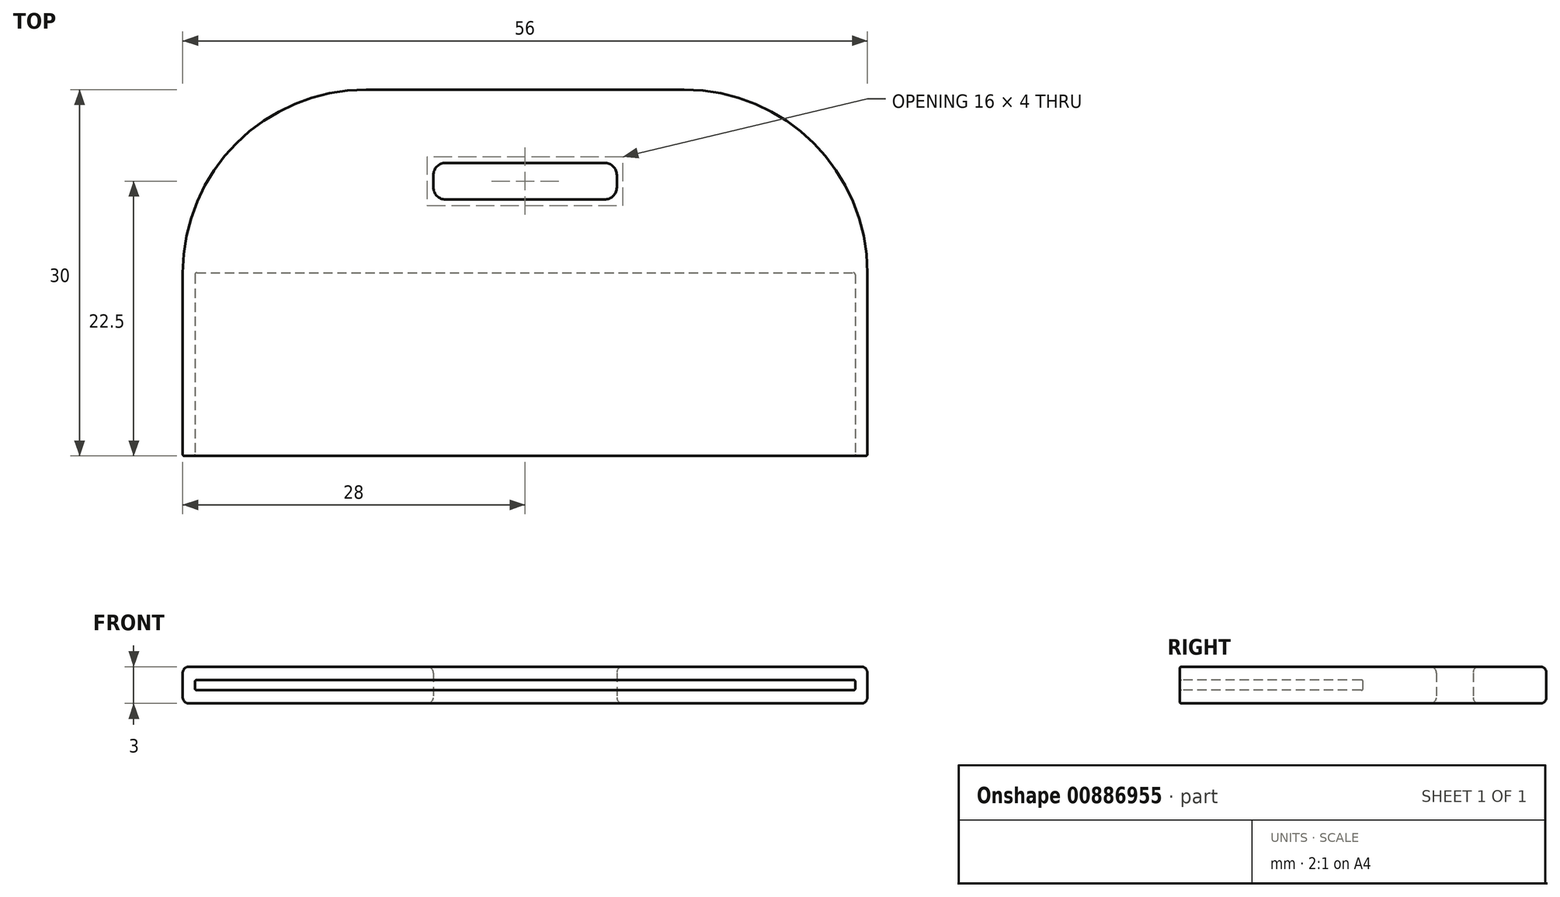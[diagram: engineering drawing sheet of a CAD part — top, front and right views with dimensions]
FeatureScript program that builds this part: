
annotation { "Feature Type Name" : "Feature", "Feature Type Description" : "" }
export const myFeature = defineFeature(function(context is Context, id is Id, definition is map)
    precondition{}
    {
        {
            var Q0;
            Q0=qCreatedBy(makeId("Top.planeOp"),FACE);
            var sketch = newSketch(context, id + "F0", { "sketchPlane" : qUnion([Q0])});
            skLineSegment(sketch, "E0.bottom", {"start": v(-28, 30) * mm, "end": v(28, 30) * mm});
            skLineSegment(sketch, "E0.top", {"start": v(-28, 0) * mm, "end": v(28, 0) * mm});
            skLineSegment(sketch, "E0.left", {"start": v(-28, 30) * mm, "end": v(-28, 0) * mm});
            skLineSegment(sketch, "E0.right", {"start": v(28, 30) * mm, "end": v(28, 0) * mm});
            skLineSegment(sketch, "E1.bottom", {"start": v(-7.5, 24) * mm, "end": v(7.5, 24) * mm});
            skLineSegment(sketch, "E1.top", {"start": v(-7.5, 21) * mm, "end": v(7.5, 21) * mm});
            skLineSegment(sketch, "E1.left", {"start": v(-7.5, 24) * mm, "end": v(-7.5, 21) * mm});
            skLineSegment(sketch, "E1.right", {"start": v(7.5, 24) * mm, "end": v(7.5, 21) * mm});
            skLineSegment(sketch, "E2", {"start": v(-7.5, 22.5) * mm, "end": v(7.5, 22.5) * mm, "construction": true});
            skLineSegment(sketch, "E3", {"start": v(0, 22.5) * mm, "end": v(0, 0) * mm, "construction": true});
            skSolve(sketch);
        }
        {
            var Q0;
            Q0 = qSketchRegion(id + "F0", true);
            extrude(context, id + "F1", {"entities" : qUnion([Q0]), "depth" : 3 * mm, "offsetDistance" : 25 * mm});
        }
        {
            var Q0;
            Q0=makeQuery(id+"F1.opExtrude","SWEPT_EDGE",EDGE,{"disambiguationData":[OSD([sQuery(id+"F0.wireOp",EDGE,"E0.bottom"),sQuery(id+"F0.wireOp",EDGE,"E0.right")])]});
            var Q1;
            Q1=makeQuery(id+"F1.opExtrude","SWEPT_EDGE",EDGE,{"disambiguationData":[OSD([sQuery(id+"F0.wireOp",EDGE,"E0.bottom"),sQuery(id+"F0.wireOp",EDGE,"E0.left")])]});
            fillet(context, id + "F2", {"entities" : qUnion([Q0, Q1]), "radius" : 15 * mm, "tangentPropagation" : true, "allowEdgeOverflow" : false});
        }
        {
            var Q0;
            Q0=makeQuery(id+"F1.opExtrude","SWEPT_EDGE",EDGE,{"disambiguationData":[OSD([sQuery(id+"F0.wireOp",EDGE,"E1.bottom"),sQuery(id+"F0.wireOp",EDGE,"E1.left")])]});
            var Q1;
            Q1=makeQuery(id+"F1.opExtrude","SWEPT_EDGE",EDGE,{"disambiguationData":[OSD([sQuery(id+"F0.wireOp",EDGE,"E1.top"),sQuery(id+"F0.wireOp",EDGE,"E1.right")])]});
            var Q2;
            Q2=makeQuery(id+"F1.opExtrude","SWEPT_EDGE",EDGE,{"disambiguationData":[OSD([sQuery(id+"F0.wireOp",EDGE,"E1.bottom"),sQuery(id+"F0.wireOp",EDGE,"E1.right")])]});
            var Q3;
            Q3=makeQuery(id+"F1.opExtrude","SWEPT_EDGE",EDGE,{"disambiguationData":[OSD([sQuery(id+"F0.wireOp",EDGE,"E1.top"),sQuery(id+"F0.wireOp",EDGE,"E1.left")])]});
            fillet(context, id + "F3", {"entities" : qUnion([Q0, Q1, Q2, Q3]), "radius" : 1 * mm, "tangentPropagation" : true, "allowEdgeOverflow" : false});
        }
        {
            var Q0;
            Q0=makeQuery(id+"F1.opExtrude","CAP_EDGE",EDGE,{"disambiguationData":[OSD([sQuery(id+"F0.wireOp",EDGE,"E0.bottom")])],"isStart":false});
            var Q1;
            Q1=makeQuery(id+"F1.opExtrude","CAP_EDGE",EDGE,{"disambiguationData":[OSD([sQuery(id+"F0.wireOp",EDGE,"E0.bottom")])],"isStart":true});
            var Q2;
            Q2=makeQuery(id+"F1.opExtrude","CAP_EDGE",EDGE,{"disambiguationData":[OSD([sQuery(id+"F0.wireOp",EDGE,"E1.bottom")])],"isStart":false});
            var Q3;
            Q3=makeQuery(id+"F1.opExtrude","CAP_EDGE",EDGE,{"disambiguationData":[OSD([sQuery(id+"F0.wireOp",EDGE,"E1.bottom")])],"isStart":true});
            fillet(context, id + "F4", {"entities" : qUnion([Q0, Q1, Q2, Q3]), "radius" : .5 * mm, "tangentPropagation" : true, "allowEdgeOverflow" : false});
        }
        {
            var Q0;
            Q0=makeQuery(id+"F1.opExtrude","SWEPT_FACE",FACE,{"disambiguationData":[OSD([sQuery(id+"F0.wireOp",EDGE,"E0.top")])]});
            var sketch = newSketch(context, id + "F5", { "sketchPlane" : qUnion([Q0])});
            skLineSegment(sketch, "E4.bottom", {"start": v(-27, 1.07) * mm, "end": v(27, 1.07) * mm});
            skLineSegment(sketch, "E4.top", {"start": v(-27, 1.93) * mm, "end": v(27, 1.93) * mm});
            skLineSegment(sketch, "E4.left", {"start": v(-27, 1.07) * mm, "end": v(-27, 1.93) * mm});
            skLineSegment(sketch, "E4.right", {"start": v(27, 1.07) * mm, "end": v(27, 1.93) * mm});
            skLineSegment(sketch, "E5", {"start": v(0, 0) * mm, "end": v(0, 1.07) * mm, "construction": true});
            skLineSegment(sketch, "E6", {"start": v(-28, 1.5) * mm, "end": v(-27, 1.5) * mm, "construction": true});
            skSolve(sketch);
        }
        {
            var Q0;
            Q0=makeQuery(id+"F5.imprint","IMPRINT",FACE,{"disambiguationData":[TD([[makeQuery(id+"F5.imprint","IMPRINT",EDGE,{"derivedFrom":sQuery(id+"F5.wireOp",EDGE,"E4.bottom")}),1.0]])]});
            extrude(context, id + "F6", {"entities" : qUnion([Q0]), "operationType" : NewBodyOperationType.REMOVE, "oppositeDirection" : true, "depth" : 15 * mm, "offsetDistance" : 25 * mm});
        }
        {
            var Q0;
            Q0=makeQuery(id+"F6.boolean.opBoolean","COPY",EDGE,{"derivedFrom":makeQuery(id+"F6.opExtrude","SWEPT_EDGE",EDGE,{"disambiguationData":[OSD([sQuery(id+"F5.wireOp",EDGE,"E4.bottom"),sQuery(id+"F5.wireOp",EDGE,"E4.left")])]})});
            var Q1;
            Q1=makeQuery(id+"F6.boolean.opBoolean","COPY",EDGE,{"derivedFrom":makeQuery(id+"F6.opExtrude","CAP_EDGE",EDGE,{"disambiguationData":[OSD([sQuery(id+"F5.wireOp",EDGE,"E4.bottom")])],"isStart":false})});
            var Q2;
            Q2=makeQuery(id+"F6.boolean.opBoolean","COPY",EDGE,{"derivedFrom":makeQuery(id+"F6.opExtrude","CAP_EDGE",EDGE,{"disambiguationData":[OSD([sQuery(id+"F5.wireOp",EDGE,"E4.left")])],"isStart":false})});
            var Q3;
            Q3=makeQuery(id+"F6.boolean.opBoolean","COPY",EDGE,{"derivedFrom":makeQuery(id+"F6.opExtrude","SWEPT_EDGE",EDGE,{"disambiguationData":[OSD([sQuery(id+"F5.wireOp",EDGE,"E4.top"),sQuery(id+"F5.wireOp",EDGE,"E4.left")])]})});
            var Q4;
            Q4=makeQuery(id+"F6.boolean.opBoolean","COPY",EDGE,{"derivedFrom":makeQuery(id+"F6.opExtrude","CAP_EDGE",EDGE,{"disambiguationData":[OSD([sQuery(id+"F5.wireOp",EDGE,"E4.top")])],"isStart":false})});
            var Q5;
            Q5=makeQuery(id+"F6.boolean.opBoolean","COPY",EDGE,{"derivedFrom":makeQuery(id+"F6.opExtrude","CAP_EDGE",EDGE,{"disambiguationData":[OSD([sQuery(id+"F5.wireOp",EDGE,"E4.right")])],"isStart":false})});
            var Q6;
            Q6=makeQuery(id+"F6.boolean.opBoolean","COPY",EDGE,{"derivedFrom":makeQuery(id+"F6.opExtrude","SWEPT_EDGE",EDGE,{"disambiguationData":[OSD([sQuery(id+"F5.wireOp",EDGE,"E4.bottom"),sQuery(id+"F5.wireOp",EDGE,"E4.right")])]})});
            var Q7;
            Q7=makeQuery(id+"F6.boolean.opBoolean","COPY",EDGE,{"derivedFrom":makeQuery(id+"F6.opExtrude","SWEPT_EDGE",EDGE,{"disambiguationData":[OSD([sQuery(id+"F5.wireOp",EDGE,"E4.top"),sQuery(id+"F5.wireOp",EDGE,"E4.right")])]})});
            var Q8;
            Q8=makeQuery(id+"F6.boolean.opBoolean","COPY",EDGE,{"derivedFrom":makeQuery(id+"F6.opExtrude","CAP_EDGE",EDGE,{"disambiguationData":[OSD([sQuery(id+"F5.wireOp",EDGE,"E4.right")])],"isStart":true})});
            var Q9;
            Q9=makeQuery(id+"F1.opExtrude","SWEPT_FACE",FACE,{"disambiguationData":[OSD([sQuery(id+"F0.wireOp",EDGE,"E0.top")])]});
            fillet(context, id + "F7", {"entities" : qUnion([Q0, Q1, Q2, Q3, Q4, Q5, Q6, Q7, Q8, Q9]), "radius" : 0.15 * mm, "tangentPropagation" : true, "allowEdgeOverflow" : false});
        }
    });
